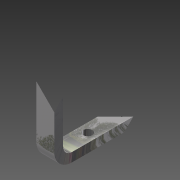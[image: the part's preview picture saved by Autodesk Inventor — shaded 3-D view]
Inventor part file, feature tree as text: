
AUTODESK INVENTOR PART (.ipt)
format: ipt  version: 2015 (Build 190159000, 159)  size: 122,368 bytes
history: native  units: mm
features: other x7, sketch x3, hole x1, fillet x1
ambient origin geometry x8: Origin, YZ Plane, XZ Plane, XY Plane, X Axis, Y Axis, Z Axis, Center Point
bodies: Body1 (feature_tree)
feature tree (12):
  other  "Bryła1"
  other  "Powierzchnia1"
  other  "Kołnierz1"
  hole  "Otwór4"  [1 undecoded]
  fillet  "Zaokrąglenie2"  Radius=10.0mm
  sketch  "Szkic1"
  other  "Płyta1"
  sketch  "Szkic2"
  sketch  "Szkic3"
  other  "Płyta2"
  other  "Gięcie1"
  other  "Narożnik1"
note: 1 required parameter value undecoded (feature->parameter linkage not recoverable at this tier; creation-order binding heuristic only, values carry confidence <= 0.55)
